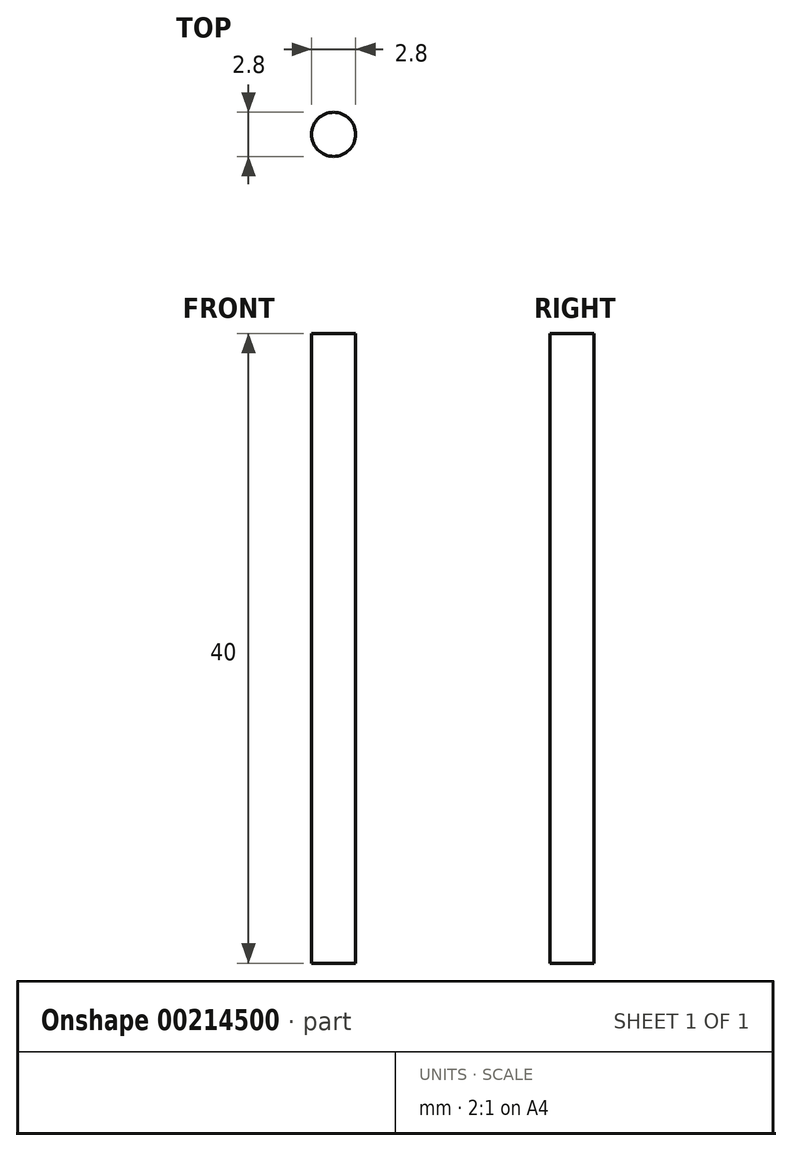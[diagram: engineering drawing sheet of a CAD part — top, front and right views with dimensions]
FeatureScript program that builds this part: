
annotation { "Feature Type Name" : "Feature", "Feature Type Description" : "" }
export const myFeature = defineFeature(function(context is Context, id is Id, definition is map)
    precondition{}
    {
        {
            var Q0;
            Q0=qCreatedBy(makeId("Top.planeOp"),FACE);
            var sketch = newSketch(context, id + "F0", { "sketchPlane" : qUnion([Q0])});
            skCircle(sketch, "E0", {"center": v(0, 0) * mm, "radius": 1.4 * mm});
            skSolve(sketch);
        }
        {
            var Q0;
            Q0=makeQuery(id+"F0.imprint","IMPRINT",FACE,{"disambiguationData":[TD([[makeQuery(id+"F0.imprint","IMPRINT",EDGE,{"derivedFrom":sQuery(id+"F0.wireOp",EDGE,"E0")}),1.0]])]});
            extrude(context, id + "F1", {"entities" : qUnion([Q0]), "depth" : 40 * mm});
        }
    });
